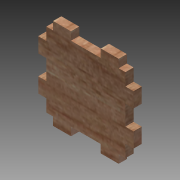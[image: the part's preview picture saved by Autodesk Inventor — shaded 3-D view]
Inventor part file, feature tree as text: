
AUTODESK INVENTOR PART (.ipt)
format: ipt  version: 2015 (Build 190159000, 159)  size: 440,832 bytes
history: native  units: mm
features: other x13, sketch x9, extrude x4
ambient origin geometry x8: Origin, YZ Plane, XZ Plane, XY Plane, X Axis, Y Axis, Z Axis, Center Point
bodies: Solid1 (feature_tree)
feature tree (26):
  other  "Blocks"
  extrude  "Extrusion1"  Depth=50.0mm
  extrude  "Extrusion3"  TaperAngle=0.0deg  [1 undecoded]
  extrude  "Extrusion10"  Depth=20.0mm
  extrude  "Extrusion11"  Depth=5.5mm
  sketch  "Sketch20"  dims[d48=8.333333mm]
  sketch  "Sketch21"  dims[d49=5.5mm d50=0.0mm d51=5.5mm d53=5.5mm d54=10.0mm d55=5.5mm d56=0.0mm d58=0.1mm d60=0.1mm d61=0.1mm d64=0.1mm d65=0.1mm d66=0.1mm d67=0.1mm d76=0.08mm]
  sketch  "Sketch19"  dims[d47=5.5mm]
  sketch  "Sketch17"  dims[d13=0.0mm]
  sketch  "Sketch18"  dims[d37=5.5mm]
  sketch  "Sketch2"  dims[d0=64.0mm d1=50.0mm]
  sketch  "Sketch4"  dims[d2=5.5mm d3=0.0mm]
  sketch  "Sketch7"  dims[d9=5.5mm d10=20.0mm]
  other  "Block1"
  sketch  "Sketch8"  dims[d11=12.0mm d12=5.5mm]
  other  "Block2"
  other  "Block3"
  other  "Block4"
  other  "Block5"
  other  "Block6"
  other  "Block7"
  other  "Block8"
  other  "Block7:1"
  other  "Block7:2"
  other  "Block8:1"
  other  "Block8:2"
note: 1 required parameter value undecoded (feature->parameter linkage not recoverable at this tier; creation-order binding heuristic only, values carry confidence <= 0.55)
